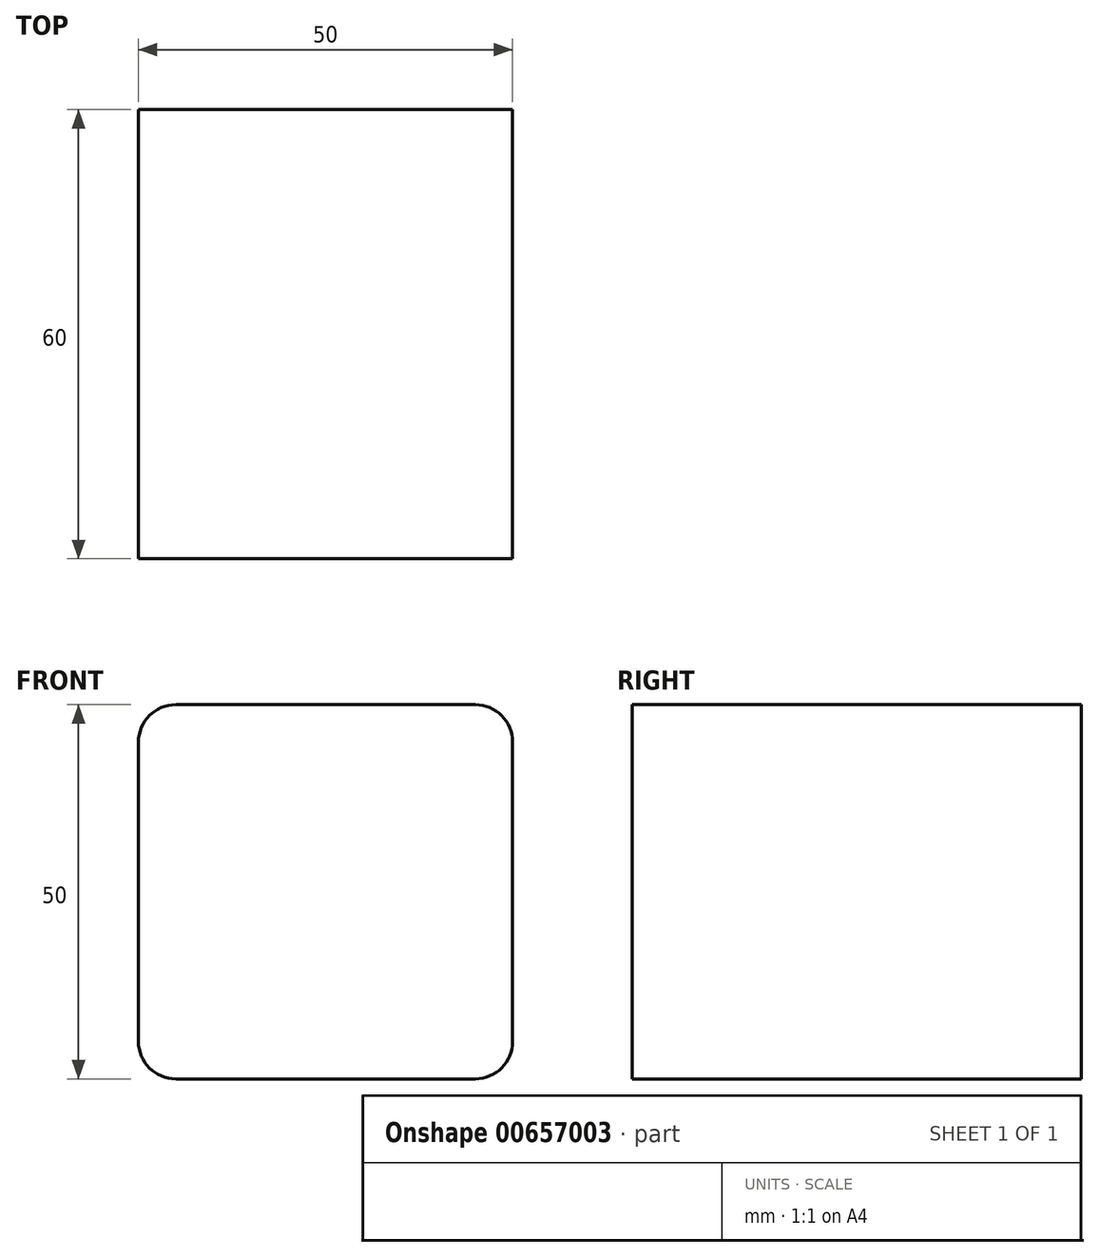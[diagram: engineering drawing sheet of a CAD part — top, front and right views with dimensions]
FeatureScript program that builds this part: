
annotation { "Feature Type Name" : "Feature", "Feature Type Description" : "" }
export const myFeature = defineFeature(function(context is Context, id is Id, definition is map)
    precondition{}
    {
        {
            var Q0;
            Q0=qCreatedBy(makeId("Front.planeOp"),FACE);
            var sketch = newSketch(context, id + "F0", { "sketchPlane" : qUnion([Q0])});
            skLineSegment(sketch, "E0.bottom", {"start": v(-127.57, 40.89) * mm, "end": v(-77.57, 40.89) * mm});
            skLineSegment(sketch, "E0.top", {"start": v(-127.57, -9.11) * mm, "end": v(-77.57, -9.11) * mm});
            skLineSegment(sketch, "E0.left", {"start": v(-127.57, 40.89) * mm, "end": v(-127.57, -9.11) * mm});
            skLineSegment(sketch, "E0.right", {"start": v(-77.57, 40.89) * mm, "end": v(-77.57, -9.11) * mm});
            skSolve(sketch);
        }
        {
            var Q0;
            Q0=makeQuery(id+"F0.imprint","IMPRINT",FACE,{"disambiguationData":[TD([[makeQuery(id+"F0.imprint","IMPRINT",EDGE,{"derivedFrom":sQuery(id+"F0.wireOp",EDGE,"E0.bottom")}),-1.0]])]});
            extrude(context, id + "F1", {"entities" : qUnion([Q0]), "depth" : 60 * mm, "offsetDistance" : 25.4 * mm});
        }
        {
            var Q0;
            Q0=makeQuery(id+"F1.opExtrude","SWEPT_EDGE",EDGE,{"disambiguationData":[OSD([sQuery(id+"F0.wireOp",EDGE,"E0.bottom"),sQuery(id+"F0.wireOp",EDGE,"E0.right")])]});
            fillet(context, id + "F2", {"entities" : qUnion([Q0]), "radius" : 5 * mm, "tangentPropagation" : true, "allowEdgeOverflow" : false});
        }
        {
            var Q0;
            Q0=makeQuery(id+"F1.opExtrude","SWEPT_EDGE",EDGE,{"disambiguationData":[OSD([sQuery(id+"F0.wireOp",EDGE,"E0.bottom"),sQuery(id+"F0.wireOp",EDGE,"E0.left")])]});
            var Q1;
            Q1=makeQuery(id+"F1.opExtrude","SWEPT_EDGE",EDGE,{"disambiguationData":[OSD([sQuery(id+"F0.wireOp",EDGE,"E0.top"),sQuery(id+"F0.wireOp",EDGE,"E0.right")])]});
            var Q2;
            Q2=makeQuery(id+"F1.opExtrude","SWEPT_EDGE",EDGE,{"disambiguationData":[OSD([sQuery(id+"F0.wireOp",EDGE,"E0.top"),sQuery(id+"F0.wireOp",EDGE,"E0.left")])]});
            fillet(context, id + "F3", {"entities" : qUnion([Q0, Q1, Q2]), "radius" : 5 * mm, "tangentPropagation" : true, "allowEdgeOverflow" : false});
        }
    });
